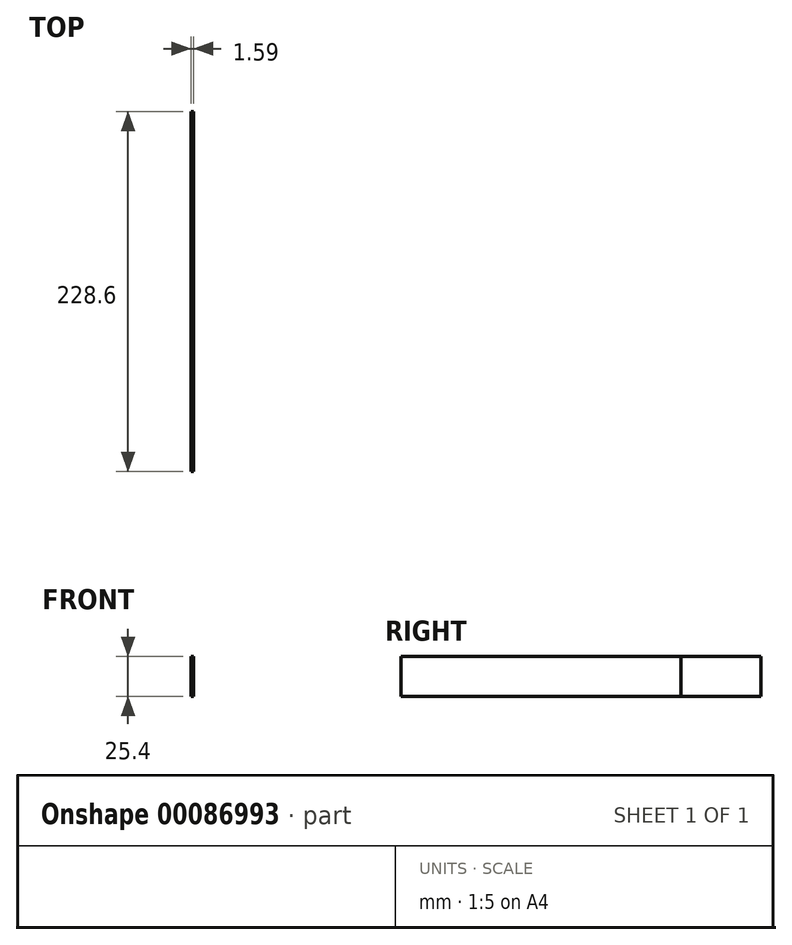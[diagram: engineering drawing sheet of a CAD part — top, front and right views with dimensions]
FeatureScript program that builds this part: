
annotation { "Feature Type Name" : "Feature", "Feature Type Description" : "" }
export const myFeature = defineFeature(function(context is Context, id is Id, definition is map)
    precondition{}
    {
        {
            var Q0;
            Q0=qCreatedBy(makeId("Front.planeOp"),FACE);
            var sketch = newSketch(context, id + "F0", { "sketchPlane" : qUnion([Q0])});
            skLineSegment(sketch, "E0.bottom", {"start": v(0, 0) * mm, "end": v(1.59, 0) * mm});
            skLineSegment(sketch, "E0.top", {"start": v(0, 25.4) * mm, "end": v(1.59, 25.4) * mm});
            skLineSegment(sketch, "E0.left", {"start": v(0, 0) * mm, "end": v(0, 25.4) * mm});
            skLineSegment(sketch, "E0.right", {"start": v(1.59, 0) * mm, "end": v(1.59, 25.4) * mm});
            skSolve(sketch);
        }
        {
            var Q0;
            Q0=qSketchRegion(id+"F0",true);
            extrude(context, id + "F1", {"entities" : qUnion([Q0]), "depth" : 228.6 * mm});
        }
        {
            var Q0;
            Q0=qSketchRegion(id+"F0",true);
            extrude(context, id + "F2", {"entities" : qUnion([Q0]), "depth" : 50.8 * mm});
        }
        {
            var Q0;
            Q0=qSketchRegion(id+"F0",true);
            extrude(context, id + "F3", {"entities" : qUnion([Q0]), "depth" : 25.4 * mm});
        }
        {
            var Q0;
            Q0=makeQuery(id+"F3.opExtrude","SWEPT_BODY",BODY,{"disambiguationData":[OSD([sQuery(id+"F0.wireOp",EDGE,"E0.bottom"),sQuery(id+"F0.wireOp",EDGE,"E0.top"),sQuery(id+"F0.wireOp",EDGE,"E0.left"),sQuery(id+"F0.wireOp",EDGE,"E0.right")])]});
            deleteBodies(context, id + "F4", {"entities" : qUnion([Q0])});
        }
    });
